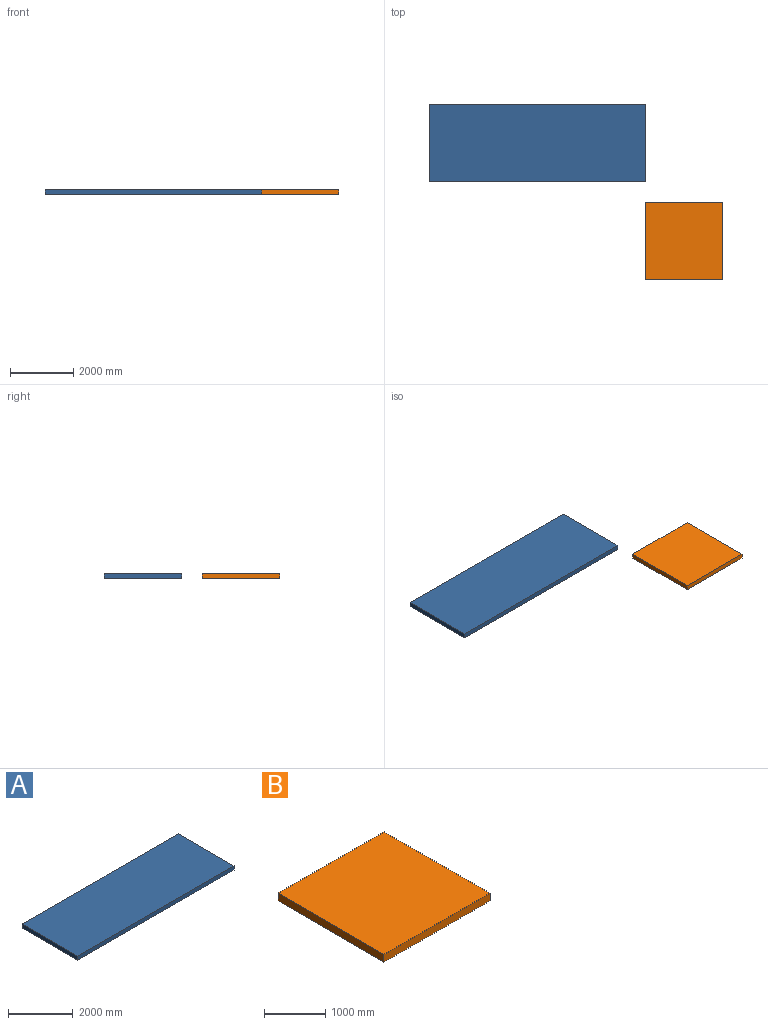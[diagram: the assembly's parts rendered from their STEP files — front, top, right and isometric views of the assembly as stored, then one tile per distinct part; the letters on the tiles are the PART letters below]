
ASSEMBLY  parts=2 mates=1
PART A: 6 faces, bbox 6832.6x2438.4x152.4 mm
  f0: plane 2438.4x152.4mm, normal (1,0,0), area 371612.2mm2, adj f1,f3,f4,f5
  f1: plane 6832.6x152.4mm, normal (0,1,0), area 1041288.2mm2, adj f0,f2,f4,f5
  f2: plane 2438.4x152.4mm, normal (-1,0,0), area 371612.2mm2, adj f1,f3,f4,f5
  f3: plane 6832.6x152.4mm, normal (0,-1,0), area 1041288.2mm2, adj f0,f2,f4,f5
  f4: plane 6832.6x2438.4mm, normal (0,0,1), area 16660611.8mm2, adj f0,f1,f2,f3
  f5: plane 6832.6x2438.4mm, normal (0,0,-1), area 16660611.8mm2, adj f0,f1,f2,f3
PART B: 6 faces, bbox 2438.4x2438.4x152.4 mm
  f0: plane 2438.4x152.4mm, normal (1,0,0), area 371612.2mm2, adj f1,f3,f4,f5
  f1: plane 2438.4x152.4mm, normal (0,1,0), area 371612.2mm2, adj f0,f2,f4,f5
  f2: plane 2438.4x152.4mm, normal (-1,0,0), area 371612.2mm2, adj f1,f3,f4,f5
  f3: plane 2438.4x152.4mm, normal (0,-1,0), area 371612.2mm2, adj f0,f2,f4,f5
  f4: plane 2438.4x2438.4mm, normal (0,0,1), area 5945794.6mm2, adj f0,f1,f2,f3
  f5: plane 2438.4x2438.4mm, normal (0,0,-1), area 5945794.6mm2, adj f0,f1,f2,f3
PLACE A at identity fixed
PLACE B t=(2438.4,-3098.8,0)mm
MATE fastened B.f4 <-> A.f4  axis (0,0,1) through (0,-3098.8,152.4)mm
